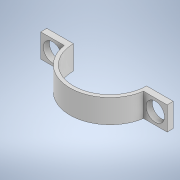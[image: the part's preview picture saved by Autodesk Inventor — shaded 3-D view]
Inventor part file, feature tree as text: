
AUTODESK INVENTOR PART (.ipt)
format: ipt  version: 2020.2 (Build 242310000, 310)  size: 128,000 bytes
history: native  units: mm
features: sketch x2, extrude x1, hole x1
ambient origin geometry x8: Origin, YZ Plane, XZ Plane, XY Plane, X Axis, Y Axis, Z Axis, Center Point
bodies: Solid1 (feature_tree)
feature tree (4):
  extrude  "Extrusion1"  Depth=17.0mm
  hole  "Hole1"  [1 undecoded]
  sketch  "Sketch1"  dims[d0=15.5mm d1=17.0mm]
  sketch  "Sketch2"  dims[d2=0.1mm d3=5.0mm d4=0.1mm d5=5.0mm d6=5.0mm d7=0.0mm d8=2.5mm d9=2.5mm d10=3.9mm d11=6.0mm d12=8.2mm d13=2.0mm d14=90.0deg d15=8.0mm d16=20.594885mm]
note: 1 required parameter value undecoded (feature->parameter linkage not recoverable at this tier; creation-order binding heuristic only, values carry confidence <= 0.55)
